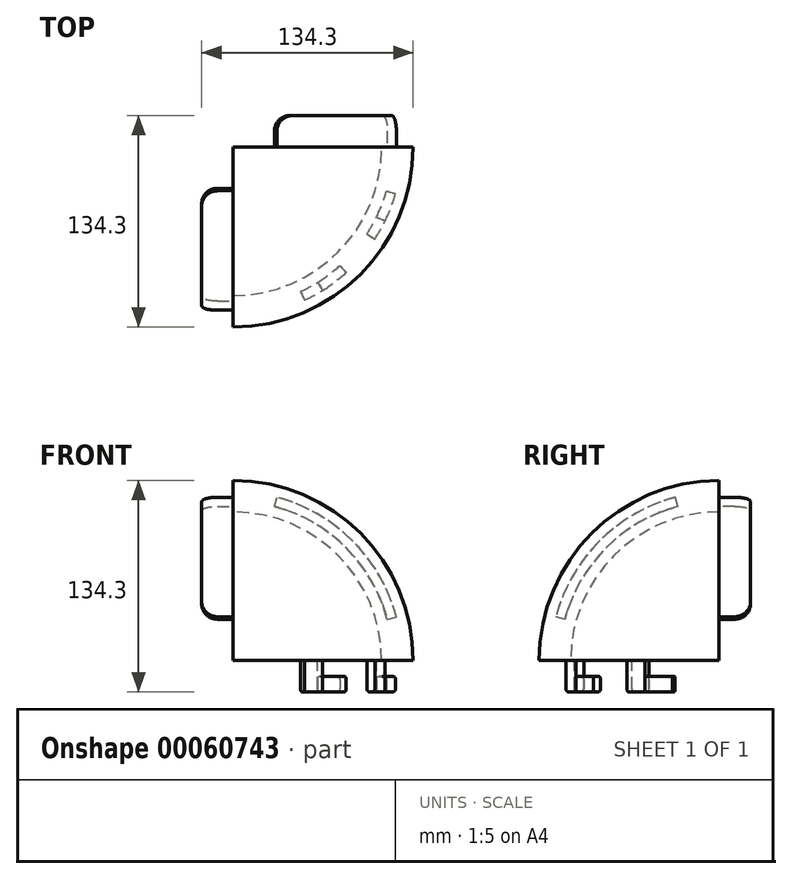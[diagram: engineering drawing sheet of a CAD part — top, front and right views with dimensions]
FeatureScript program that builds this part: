
annotation { "Feature Type Name" : "Feature", "Feature Type Description" : "" }
export const myFeature = defineFeature(function(context is Context, id is Id, definition is map)
    precondition{}
    {
        {
            var Q0;
            Q0=qCreatedBy(makeId("Right.planeOp"),FACE);
            var sketch = newSketch(context, id + "F0", { "sketchPlane" : qUnion([Q0])});
            skArc(sketch, "E0", {"start": v(0, 114.3) * mm, "mid": v(-80.82, 80.82) * mm, "end": v(-114.3, 0) * mm});
            skArc(sketch, "E1", {"start": v(0, 94.3) * mm, "mid": v(-66.68, 66.68) * mm, "end": v(-94.3, 0) * mm});
            skLineSegment(sketch, "E2", {"start": v(0, 94.3) * mm, "end": v(0, 114.3) * mm});
            skLineSegment(sketch, "E3", {"start": v(-94.3, 0) * mm, "end": v(-114.3, 0) * mm});
            skSolve(sketch);
        }
        {
            var Q0;
            Q0=makeQuery(id+"F0.imprint","IMPRINT",FACE,{"disambiguationData":[TD([[makeQuery(id+"F0.imprint","IMPRINT",EDGE,{"derivedFrom":sQuery(id+"F0.wireOp",EDGE,"E0")}),1.0]])]});
            var Q1;
            Q1=sQuery(id+"F0.wireOp",EDGE,"E2");
            revolve(context, id + "F1", {"entities" : qUnion([Q0]), "axis" : qUnion([Q1]), "revolveType" : RevolveType.ONE_DIRECTION, "angle" : 90 * degree});
        }
        {
            var Q0;
            Q0=makeQuery(id+"F1.opRevolve","CAP_FACE",FACE,{"disambiguationData":[OSD([sQuery(id+"F0.wireOp",EDGE,"E0"),sQuery(id+"F0.wireOp",EDGE,"E1"),sQuery(id+"F0.wireOp",EDGE,"E2"),sQuery(id+"F0.wireOp",EDGE,"E3")])],"isStart":false});
            var sketch = newSketch(context, id + "F2", { "sketchPlane" : qUnion([Q0])});
            skArc(sketch, "E4", {"start": v(-27.77, 103.64) * mm, "mid": v(-75.87, 75.87) * mm, "end": v(-103.64, 27.77) * mm});
            skArc(sketch, "E5", {"start": v(-26.22, 97.85) * mm, "mid": v(-71.63, 71.63) * mm, "end": v(-97.85, 26.22) * mm});
            skLineSegment(sketch, "E6", {"start": v(0, 0) * mm, "end": v(-27.77, 103.64) * mm});
            skLineSegment(sketch, "E7", {"start": v(-97.85, 26.22) * mm, "end": v(-103.64, 27.77) * mm});
            skSolve(sketch);
        }
        {
            var Q0;
            Q0=makeQuery(id+"F2.imprint","IMPRINT",FACE,{"disambiguationData":[TD([[makeQuery(id+"F2.imprint","IMPRINT",EDGE,{"derivedFrom":sQuery(id+"F2.wireOp",EDGE,"E4")}),1.0]])]});
            extrude(context, id + "F3", {"entities" : qUnion([Q0]), "operationType" : NewBodyOperationType.ADD, "depth" : 20 * mm});
        }
        {
            var Q0;
            Q0=makeQuery(id+"F0.imprint","IMPRINT",FACE,{"disambiguationData":[TD([[makeQuery(id+"F0.imprint","IMPRINT",EDGE,{"derivedFrom":sQuery(id+"F0.wireOp",EDGE,"E0")}),1.0]])]});
            var sketch = newSketch(context, id + "F4", { "sketchPlane" : qUnion([Q0])});
            skArc(sketch, "E8.0", {"start": v(-26.22, 97.85) * mm, "mid": v(-71.63, 71.63) * mm, "end": v(-97.85, 26.22) * mm});
            skArc(sketch, "E9.0", {"start": v(-27.77, 103.64) * mm, "mid": v(-75.87, 75.87) * mm, "end": v(-103.64, 27.77) * mm});
            skLineSegment(sketch, "E10", {"start": v(-26.22, 97.85) * mm, "end": v(-27.77, 103.64) * mm});
            skLineSegment(sketch, "E11", {"start": v(-97.85, 26.22) * mm, "end": v(-103.64, 27.77) * mm});
            skSolve(sketch);
        }
        {
            var Q0;
            Q0=makeQuery(id+"F4.imprint","IMPRINT",FACE,{"disambiguationData":[TD([[makeQuery(id+"F4.imprint","IMPRINT",EDGE,{"derivedFrom":sQuery(id+"F4.wireOp",EDGE,"E8.0")}),-1.0]])]});
            extrude(context, id + "F5", {"entities" : qUnion([Q0]), "operationType" : NewBodyOperationType.ADD, "oppositeDirection" : true, "depth" : 20 * mm});
        }
        {
            var Q0;
            Q0=makeQuery(id+"F5.boolean.opBoolean","MERGE",FACE,{"derivedFrom":[makeQuery(id+"F3.boolean.opBoolean","MERGE",FACE,{"derivedFrom":[makeQuery(id+"F1.opRevolve","SWEPT_FACE",FACE,{"disambiguationData":[OSD([sQuery(id+"F0.wireOp",EDGE,"E3")])]}),makeQuery(id+"F3.opExtrude","SWEPT_FACE",FACE,{"disambiguationData":[OSD([sQuery(id+"F2.wireOp",EDGE,"tj54Cu89-9J1S-AJKw-QeEM-ljXHSpR1f2pj")])]})]}),makeQuery(id+"F5.opExtrude","SWEPT_FACE",FACE,{"disambiguationData":[OSD([sQuery(id+"F4.wireOp",EDGE,"EMUQLBOC-9Rso-lLbz-JRUg-i4oPmn0DbPj1")])]})]});
            var sketch = newSketch(context, id + "F6", { "sketchPlane" : qUnion([Q0])});
            skArc(sketch, "E12", {"start": v(91.05, 44.4) * mm, "mid": v(88.17, 49.88) * mm, "end": v(84.96, 55.17) * mm});
            skArc(sketch, "E13", {"start": v(96.44, 47.04) * mm, "mid": v(93.39, 52.84) * mm, "end": v(89.99, 58.44) * mm});
            skLineSegment(sketch, "E14", {"start": v(42.81, 91.8) * mm, "end": v(45.35, 97.25) * mm});
            skLineSegment(sketch, "E15", {"start": v(53.68, 85.9) * mm, "end": v(56.86, 91) * mm});
            skLineSegment(sketch, "E16", {"start": v(84.96, 55.17) * mm, "end": v(89.99, 58.44) * mm});
            skLineSegment(sketch, "E17", {"start": v(91.05, 44.4) * mm, "end": v(96.44, 47.04) * mm});
            skArc(sketch, "E18.trimOffspring", {"start": v(53.68, 85.9) * mm, "mid": v(48.34, 89.02) * mm, "end": v(42.81, 91.8) * mm});
            skArc(sketch, "E19.trimOffspring", {"start": v(56.86, 91) * mm, "mid": v(51.2, 94.3) * mm, "end": v(45.35, 97.25) * mm});
            skSolve(sketch);
        }
        {
            var Q0;
            Q0=makeQuery(id+"F6.imprint","IMPRINT",FACE,{"disambiguationData":[TD([[makeQuery(id+"F6.imprint","IMPRINT",EDGE,{"derivedFrom":sQuery(id+"F6.wireOp",EDGE,"E14")}),-1.0]])]});
            var Q1;
            Q1=makeQuery(id+"F6.imprint","IMPRINT",FACE,{"disambiguationData":[TD([[makeQuery(id+"F6.imprint","IMPRINT",EDGE,{"derivedFrom":sQuery(id+"F6.wireOp",EDGE,"E12")}),-1.0]])]});
            extrude(context, id + "F7", {"entities" : qUnion([Q0, Q1]), "operationType" : NewBodyOperationType.ADD, "depth" : 20 * mm});
        }
        {
            var Q0;
            Q0=makeQuery(id+"F7.opExtrude","CAP_FACE",FACE,{"disambiguationData":[OSD([sQuery(id+"F6.wireOp",EDGE,"E14"),sQuery(id+"F6.wireOp",EDGE,"E15"),sQuery(id+"F6.wireOp",EDGE,"E18.trimOffspring"),sQuery(id+"F6.wireOp",EDGE,"E19.trimOffspring")])],"isStart":false});
            var sketch = newSketch(context, id + "F8", { "sketchPlane" : qUnion([Q0])});
            skArc(sketch, "E20", {"start": v(67.78, 75.28) * mm, "mid": v(60.96, 80.9) * mm, "end": v(53.68, 85.9) * mm});
            skArc(sketch, "E21", {"start": v(71.8, 79.74) * mm, "mid": v(64.57, 85.7) * mm, "end": v(56.86, 91) * mm});
            skLineSegment(sketch, "E22", {"start": v(53.68, 85.9) * mm, "end": v(56.86, 91) * mm});
            skLineSegment(sketch, "E23", {"start": v(67.78, 75.28) * mm, "end": v(71.8, 79.74) * mm});
            skSolve(sketch);
        }
        {
            var Q0;
            Q0=makeQuery(id+"F8.imprint","IMPRINT",FACE,{"disambiguationData":[TD([[makeQuery(id+"F8.imprint","IMPRINT",EDGE,{"derivedFrom":sQuery(id+"F8.wireOp",EDGE,"E20")}),-1.0]])]});
            extrude(context, id + "F9", {"entities" : qUnion([Q0]), "oppositeDirection" : true, "depth" : 10 * mm});
        }
        {
            var Q0;
            Q0=makeQuery(id+"F7.opExtrude","CAP_FACE",FACE,{"disambiguationData":[OSD([sQuery(id+"F6.wireOp",EDGE,"E12"),sQuery(id+"F6.wireOp",EDGE,"E13"),sQuery(id+"F6.wireOp",EDGE,"E16"),sQuery(id+"F6.wireOp",EDGE,"E17")])],"isStart":false});
            var sketch = newSketch(context, id + "F10", { "sketchPlane" : qUnion([Q0])});
            skArc(sketch, "E24", {"start": v(97.38, 27.92) * mm, "mid": v(94.57, 36.3) * mm, "end": v(91.05, 44.4) * mm});
            skArc(sketch, "E25", {"start": v(103.14, 29.58) * mm, "mid": v(100.17, 38.45) * mm, "end": v(96.44, 47.04) * mm});
            skLineSegment(sketch, "E26", {"start": v(91.05, 44.4) * mm, "end": v(96.44, 47.04) * mm});
            skLineSegment(sketch, "E27", {"start": v(97.38, 27.92) * mm, "end": v(103.14, 29.58) * mm});
            skSolve(sketch);
        }
        {
            var Q0;
            Q0=makeQuery(id+"F10.imprint","IMPRINT",FACE,{"disambiguationData":[TD([[makeQuery(id+"F10.imprint","IMPRINT",EDGE,{"derivedFrom":sQuery(id+"F10.wireOp",EDGE,"E24")}),-1.0]])]});
            extrude(context, id + "F11", {"entities" : qUnion([Q0]), "oppositeDirection" : true, "depth" : 10 * mm});
        }
        {
            var Q0;
            Q0=makeQuery(id+"F7.opExtrude","CAP_EDGE",EDGE,{"disambiguationData":[OSD([sQuery(id+"F6.wireOp",EDGE,"E19.trimOffspring")])],"isStart":false});
            var Q1;
            Q1=makeQuery(id+"F7.opExtrude","CAP_EDGE",EDGE,{"disambiguationData":[OSD([sQuery(id+"F6.wireOp",EDGE,"E18.trimOffspring")])],"isStart":false});
            var Q2;
            Q2=makeQuery(id+"F9.opExtrude","CAP_EDGE",EDGE,{"disambiguationData":[OSD([sQuery(id+"F8.wireOp",EDGE,"E20")])],"isStart":true});
            var Q3;
            Q3=makeQuery(id+"F9.opExtrude","CAP_EDGE",EDGE,{"disambiguationData":[OSD([sQuery(id+"F8.wireOp",EDGE,"E21")])],"isStart":true});
            var Q4;
            Q4=makeQuery(id+"F7.opExtrude","CAP_EDGE",EDGE,{"disambiguationData":[OSD([sQuery(id+"F6.wireOp",EDGE,"E12")])],"isStart":false});
            var Q5;
            Q5=makeQuery(id+"F11.opExtrude","CAP_EDGE",EDGE,{"disambiguationData":[OSD([sQuery(id+"F10.wireOp",EDGE,"E24")])],"isStart":true});
            var Q6;
            Q6=makeQuery(id+"F11.opExtrude","CAP_EDGE",EDGE,{"disambiguationData":[OSD([sQuery(id+"F10.wireOp",EDGE,"E25")])],"isStart":true});
            var Q7;
            Q7=makeQuery(id+"F7.opExtrude","CAP_EDGE",EDGE,{"disambiguationData":[OSD([sQuery(id+"F6.wireOp",EDGE,"E13")])],"isStart":false});
            var Q8;
            Q8=makeQuery(id+"F9.opExtrude","CAP_EDGE",EDGE,{"disambiguationData":[OSD([sQuery(id+"F8.wireOp",EDGE,"E21")])],"isStart":false});
            var Q9;
            Q9=makeQuery(id+"F9.opExtrude","CAP_EDGE",EDGE,{"disambiguationData":[OSD([sQuery(id+"F8.wireOp",EDGE,"E20")])],"isStart":false});
            var Q10;
            Q10=makeQuery(id+"F11.opExtrude","CAP_EDGE",EDGE,{"disambiguationData":[OSD([sQuery(id+"F10.wireOp",EDGE,"E25")])],"isStart":false});
            var Q11;
            Q11=makeQuery(id+"F11.opExtrude","CAP_EDGE",EDGE,{"disambiguationData":[OSD([sQuery(id+"F10.wireOp",EDGE,"E24")])],"isStart":false});
            fillet(context, id + "F12", {"entities" : qUnion([Q0, Q1, Q2, Q3, Q4, Q5, Q6, Q7, Q8, Q9, Q10, Q11]), "radius" : 2 * mm, "tangentPropagation" : true, "allowEdgeOverflow" : false});
        }
        {
            var Q0;
            Q0=makeQuery(id+"F3.opExtrude","CAP_EDGE",EDGE,{"disambiguationData":[OSD([sQuery(id+"F2.wireOp",EDGE,"E7")])],"isStart":false});
            var Q1;
            Q1=makeQuery(id+"F3.opExtrude","CAP_EDGE",EDGE,{"disambiguationData":[OSD([sQuery(id+"F2.wireOp",EDGE,"E6")])],"isStart":false});
            var Q2;
            Q2=makeQuery(id+"F5.opExtrude","CAP_EDGE",EDGE,{"disambiguationData":[OSD([sQuery(id+"F4.wireOp",EDGE,"E10")])],"isStart":false});
            var Q3;
            Q3=makeQuery(id+"F5.opExtrude","CAP_EDGE",EDGE,{"disambiguationData":[OSD([sQuery(id+"F4.wireOp",EDGE,"E11")])],"isStart":false});
            fillet(context, id + "F13", {"entities" : qUnion([Q0, Q1, Q2, Q3]), "radius" : 10 * mm, "tangentPropagation" : true, "allowEdgeOverflow" : false});
        }
    });
